# Revit family: Gus-Branch_Layout_01-Teknion-R2018
name_source: partatom
category: Furniture Systems
revit_build: Autodesk Revit 2018 (Build: 20190510_1515(x64)
units: mm (PartAtom-declared; Revit-internal decimal feet)

## family parameters
Always vertical = Yes
Cut with Voids When Loaded = No
OmniClass Number = 23.40.70.14.64.21
OmniClass Title = Systems Furniture
Part Type = Normal
Room Calculation Point = No
Round Connector Dimension = Use Diameter
Shared = Yes
Work Plane-Based = Yes

## types (1)
- Branch 01
    Assembly Code = E2020200
    Default Elevation = 4' - 0"
    Description = 3'-8" x 2'-9" Overall
    Manufacturer = Teknion
    Manufacturer Fax = 416.534.2452
    Model = Gus - Branch Layout 01
    Product Line = Gus Modern
    Product Page URL = https://www.teknionplanningtool.com
    Series = Gus Modern
    URL = http://www.teknion.com
    Warranty = https://d2r72yk5wmppdj.cloudfront.net

## geometry (parser evidence)
native form markers: Sweep x22
no freeform markers — native parametric forms only
